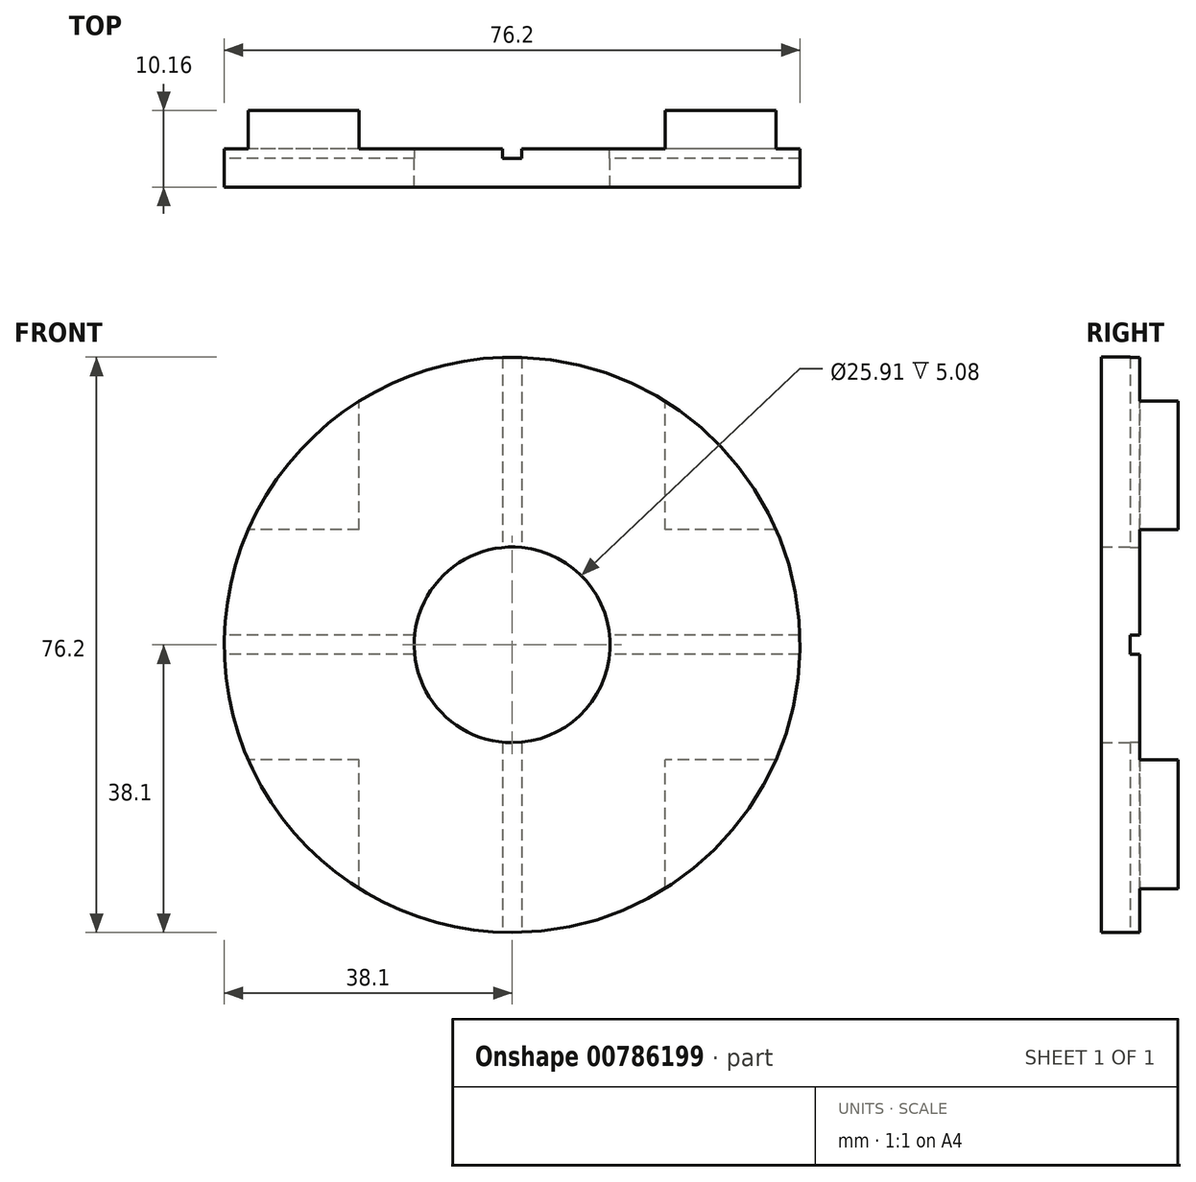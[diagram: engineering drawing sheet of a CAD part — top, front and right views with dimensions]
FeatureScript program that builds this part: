
annotation { "Feature Type Name" : "Feature", "Feature Type Description" : "" }
export const myFeature = defineFeature(function(context is Context, id is Id, definition is map)
    precondition{}
    {
        {
            var Q0;
            Q0=qCreatedBy(makeId("Front.planeOp"),FACE);
            var sketch = newSketch(context, id + "F0", { "sketchPlane" : qUnion([Q0])});
            skCircle(sketch, "E0", {"center": v(0, 0) * mm, "radius": 12.7 * mm});
            skSolve(sketch);
        }
        {
            var Q0;
            Q0=qSketchRegion(id+"F0",true);
            extrude(context, id + "F1", {"entities" : qUnion([Q0]), "depth" : 17.78 * mm, "offsetDistance" : 25.4 * mm});
        }
        {
            var Q0;
            Q0=qCreatedBy(makeId("Front.planeOp"),FACE);
            var sketch = newSketch(context, id + "F2", { "sketchPlane" : qUnion([Q0])});
            skCircle(sketch, "E1", {"center": v(0, 0) * mm, "radius": 38.1 * mm});
            skSolve(sketch);
        }
        {
            var Q0;
            Q0=qSketchRegion(id+"F2",true);
            extrude(context, id + "F3", {"entities" : qUnion([Q0]), "operationType" : NewBodyOperationType.ADD, "depth" : 10.16 * mm, "offsetDistance" : 25.4 * mm});
        }
        {
            var Q0;
            Q0=qCreatedBy(makeId("Front.planeOp"),FACE);
            var sketch = newSketch(context, id + "F4", { "sketchPlane" : qUnion([Q0])});
            skCircle(sketch, "E2", {"center": v(0, 0) * mm, "radius": 12.95 * mm});
            skSolve(sketch);
        }
        {
            var Q0;
            Q0=qSketchRegion(id+"F4",true);
            extrude(context, id + "F5", {"entities" : qUnion([Q0]), "operationType" : NewBodyOperationType.REMOVE, "endBound" : BoundingType.THROUGH_ALL, "depth" : 25.4 * mm, "offsetDistance" : 25.4 * mm, "hasSecondDirection" : true, "secondDirectionBound" : SecondDirectionBoundingType.THROUGH_ALL, "secondDirectionOppositeDirection" : true, "secondDirectionDepth" : 25.4 * mm});
        }
        {
            var Q0;
            Q0=qCreatedBy(makeId("Right.planeOp"),FACE);
            var sketch = newSketch(context, id + "F6", { "sketchPlane" : qUnion([Q0])});
            skLineSegment(sketch, "E3.bottom", {"start": v(0, 15.24) * mm, "end": v(-5.08, 15.24) * mm});
            skLineSegment(sketch, "E3.top", {"start": v(0, -15.24) * mm, "end": v(-5.08, -15.24) * mm});
            skLineSegment(sketch, "E3.left", {"start": v(0, 15.24) * mm, "end": v(0, -15.24) * mm});
            skLineSegment(sketch, "E3.right", {"start": v(-5.08, 15.24) * mm, "end": v(-5.08, -15.24) * mm});
            skSolve(sketch);
        }
        {
            var Q0;
            Q0=qSketchRegion(id+"F6",true);
            extrude(context, id + "F7", {"entities" : qUnion([Q0]), "operationType" : NewBodyOperationType.REMOVE, "endBound" : BoundingType.THROUGH_ALL, "depth" : 25.4 * mm, "offsetDistance" : 25.4 * mm, "hasSecondDirection" : true, "secondDirectionBound" : SecondDirectionBoundingType.THROUGH_ALL, "secondDirectionOppositeDirection" : true, "secondDirectionDepth" : 25.4 * mm});
        }
        {
            var Q0;
            Q0=qCreatedBy(makeId("Top.planeOp"),FACE);
            var sketch = newSketch(context, id + "F8", { "sketchPlane" : qUnion([Q0])});
            skLineSegment(sketch, "E4.bottom", {"start": v(-20.26, 0) * mm, "end": v(20.26, 0) * mm});
            skLineSegment(sketch, "E4.top", {"start": v(-20.26, -5.08) * mm, "end": v(20.26, -5.08) * mm});
            skLineSegment(sketch, "E4.left", {"start": v(-20.26, 0) * mm, "end": v(-20.26, -5.08) * mm});
            skLineSegment(sketch, "E4.right", {"start": v(20.26, 0) * mm, "end": v(20.26, -5.08) * mm});
            skSolve(sketch);
        }
        {
            var Q0;
            Q0=qSketchRegion(id+"F8",true);
            extrude(context, id + "F9", {"entities" : qUnion([Q0]), "operationType" : NewBodyOperationType.REMOVE, "endBound" : BoundingType.THROUGH_ALL, "oppositeDirection" : true, "depth" : 25.4 * mm, "offsetDistance" : 25.4 * mm, "hasSecondDirection" : true, "secondDirectionBound" : SecondDirectionBoundingType.THROUGH_ALL, "secondDirectionOppositeDirection" : false, "secondDirectionDepth" : 25.4 * mm});
        }
        {
            var Q0;
            {var subQ0=sQuery(id+"F2.wireOp",EDGE,"E1");var subQ2=makeQuery(id+"F7.opExtrude","SWEPT_FACE",FACE,{"disambiguationData":[OSD([sQuery(id+"F6.wireOp",EDGE,"E3.bottom")])]});Q0=makeQuery(id+"F9.boolean.opBoolean","SPLIT",FACE,{"disambiguationData":[TD([makeQuery(id+"F7.boolean.opBoolean","COPY",FACE,{"disambiguationData":[OD(1.0)],"derivedFrom":subQ2})])],"derivedFrom":makeQuery(id+"F7.boolean.opBoolean","SPLIT",FACE,{"disambiguationData":[TD([subQ2])],"derivedFrom":makeQuery(id+"F3.boolean.opBoolean","MERGE",FACE,{"derivedFrom":[makeQuery(id+"F1.opExtrude","CAP_FACE",FACE,{"disambiguationData":[OSD([sQuery(id+"F0.wireOp",EDGE,"E0")])],"isStart":true}),makeQuery(id+"F3.opExtrude","CAP_FACE",FACE,{"disambiguationData":[OSD([subQ0])],"isStart":true})]})})});}
            var sketch = newSketch(context, id + "F10", { "sketchPlane" : qUnion([Q0])});
            skArc(sketch, "E5.0", {"start": v(38.08, -1.27) * mm, "mid": v(38.1, 0) * mm, "end": v(38.08, 1.27) * mm});
            skLineSegment(sketch, "E6.left", {"start": v(-1.27, 38.08) * mm, "end": v(-1.27, 1.27) * mm});
            skLineSegment(sketch, "E6.right", {"start": v(1.27, 38.08) * mm, "end": v(1.27, 1.27) * mm});
            skLineSegment(sketch, "E7.bottom", {"start": v(-38.08, 1.27) * mm, "end": v(-1.27, 1.27) * mm});
            skLineSegment(sketch, "E7.top", {"start": v(-38.08, -1.27) * mm, "end": v(-1.27, -1.27) * mm});
            skLineSegment(sketch, "E8.trimOffspring", {"start": v(1.27, 1.27) * mm, "end": v(38.08, 1.27) * mm});
            skLineSegment(sketch, "E9.trimOffspring", {"start": v(-1.27, -1.27) * mm, "end": v(-1.27, -38.08) * mm});
            skLineSegment(sketch, "E10.trimOffspring", {"start": v(1.27, -1.27) * mm, "end": v(38.08, -1.27) * mm});
            skLineSegment(sketch, "E11.trimOffspring", {"start": v(1.27, -1.27) * mm, "end": v(1.27, -38.08) * mm});
            skArc(sketch, "E12.trimOffspring", {"start": v(-1.27, -38.08) * mm, "mid": v(0, -38.1) * mm, "end": v(1.27, -38.08) * mm});
            skArc(sketch, "E13.trimOffspring", {"start": v(-38.08, 1.27) * mm, "mid": v(-38.1, 0) * mm, "end": v(-38.08, -1.27) * mm});
            skArc(sketch, "E14.trimOffspring", {"start": v(1.27, 38.08) * mm, "mid": v(0, 38.1) * mm, "end": v(-1.27, 38.08) * mm});
            skSolve(sketch);
        }
        {
            var Q0;
            Q0=qSketchRegion(id+"F10",true);
            extrude(context, id + "F11", {"entities" : qUnion([Q0]), "operationType" : NewBodyOperationType.REMOVE, "oppositeDirection" : true, "depth" : 6.35 * mm, "offsetDistance" : 25.4 * mm});
        }
    });
